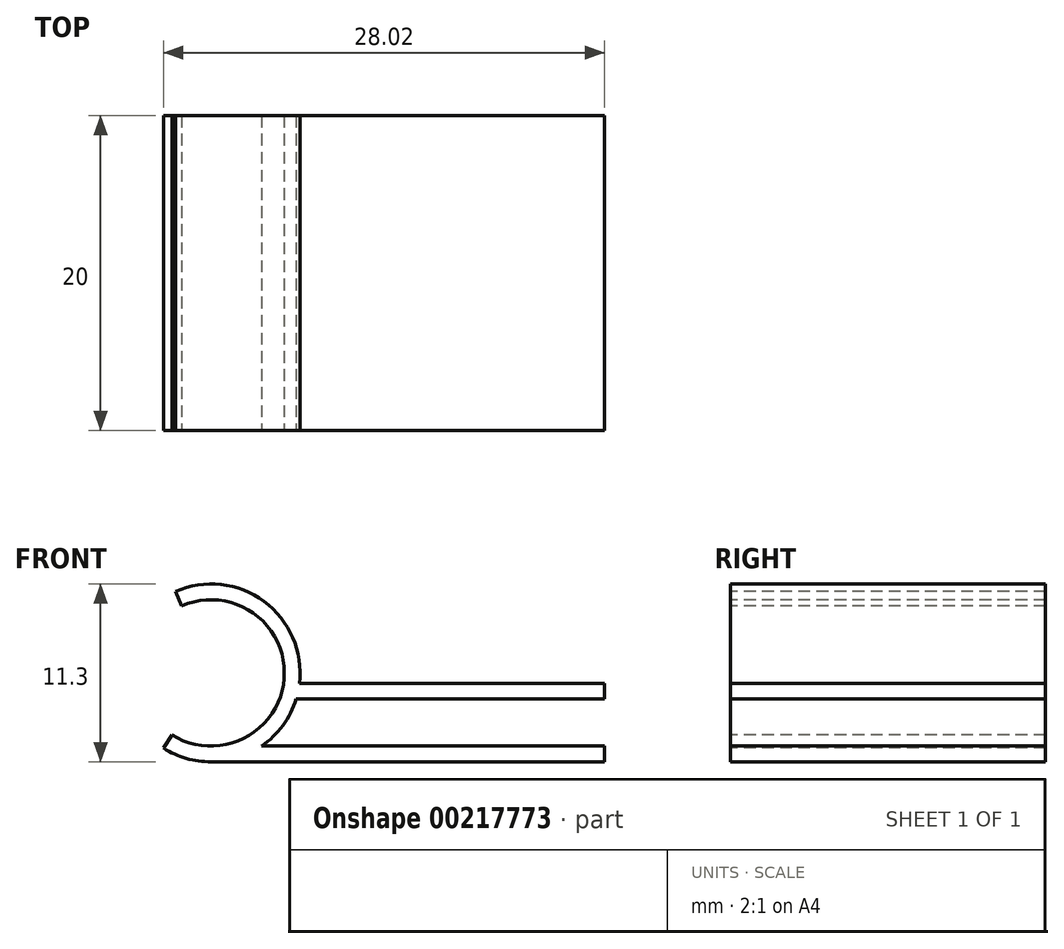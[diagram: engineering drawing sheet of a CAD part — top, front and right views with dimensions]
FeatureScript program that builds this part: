
annotation { "Feature Type Name" : "Feature", "Feature Type Description" : "" }
export const myFeature = defineFeature(function(context is Context, id is Id, definition is map)
    precondition{}
    {
        {
            var Q0;
            Q0=qCreatedBy(makeId("Front.planeOp"),FACE);
            var sketch = newSketch(context, id + "F0", { "sketchPlane" : qUnion([Q0])});
            skCircle(sketch, "E0", {"center": v(11.88, 1.65) * mm, "radius": 4.65 * mm});
            skCircle(sketch, "E1", {"center": v(11.88, 1.65) * mm, "radius": 5.65 * mm});
            skLineSegment(sketch, "E2.bottom", {"start": v(11.88, -4) * mm, "end": v(36.88, -4) * mm});
            skLineSegment(sketch, "E2.top", {"start": v(11.88, -3) * mm, "end": v(36.88, -3) * mm});
            skLineSegment(sketch, "E2.left", {"start": v(11.88, -4) * mm, "end": v(11.88, -3) * mm});
            skLineSegment(sketch, "E2.right", {"start": v(36.88, -4) * mm, "end": v(36.88, -3) * mm});
            skLineSegment(sketch, "E3.bottom", {"start": v(36.88, 0) * mm, "end": v(16.49, 0) * mm});
            skLineSegment(sketch, "E3.top", {"start": v(36.88, 1) * mm, "end": v(16.49, 1) * mm});
            skLineSegment(sketch, "E3.left", {"start": v(36.88, 0) * mm, "end": v(36.88, 1) * mm});
            skLineSegment(sketch, "E3.right", {"start": v(16.49, 0) * mm, "end": v(16.49, 1) * mm});
            skLineSegment(sketch, "E4", {"start": v(6.8, 13.29) * mm, "end": v(11.88, 1.65) * mm});
            skLineSegment(sketch, "E5", {"start": v(11.88, 1.65) * mm, "end": v(5.08, -9.07) * mm});
            skLineSegment(sketch, "E6", {"start": v(6.8, 13.29) * mm, "end": v(5.08, -9.07) * mm});
            skSolve(sketch);
        }
        {
            var Q0;
            {var subQ3=sQuery(id+"F0.wireOp",EDGE,"E4");var subQ5=sQuery(id+"F0.wireOp",EDGE,"E1");var subQ6=makeQuery(id+"F0.imprint","INTERSECT",VERTEX,{"derivedFrom":[subQ5,subQ3]});Q0=makeQuery(id+"F0.imprint","IMPRINT",FACE,{"disambiguationData":[TD([[makeQuery(id+"F0.imprint","IMPRINT",EDGE,{"disambiguationData":[TD([[subQ6,1.0]])],"derivedFrom":subQ5}),1.0]])]});}
            var Q1;
            {var subQ7=sQuery(id+"F0.wireOp",EDGE,"E3.right");Q1=makeQuery(id+"F0.imprint","IMPRINT",FACE,{"disambiguationData":[TD([[makeQuery(id+"F0.imprint","IMPRINT",EDGE,{"derivedFrom":subQ7}),1.0]])]});}
            var Q2;
            {var subQ5=sQuery(id+"F0.wireOp",EDGE,"E3.right");Q2=makeQuery(id+"F0.imprint","IMPRINT",FACE,{"disambiguationData":[TD([[makeQuery(id+"F0.imprint","IMPRINT",EDGE,{"derivedFrom":subQ5}),-1.0]])]});}
            var Q3;
            {var subQ5=sQuery(id+"F0.wireOp",EDGE,"E3.left");Q3=makeQuery(id+"F0.imprint","IMPRINT",FACE,{"disambiguationData":[TD([[makeQuery(id+"F0.imprint","IMPRINT",EDGE,{"derivedFrom":subQ5}),1.0]])]});}
            var Q4;
            {var subQ0=sQuery(id+"F0.wireOp",EDGE,"E2.bottom");Q4=makeQuery(id+"F0.imprint","IMPRINT",FACE,{"disambiguationData":[TD([[makeQuery(id+"F0.imprint","IMPRINT",EDGE,{"derivedFrom":subQ0}),1.0]])]});}
            var Q5;
            {var subQ0=sQuery(id+"F0.wireOp",EDGE,"E2.left");Q5=makeQuery(id+"F0.imprint","IMPRINT",FACE,{"disambiguationData":[TD([[makeQuery(id+"F0.imprint","IMPRINT",EDGE,{"derivedFrom":subQ0}),-1.0]])]});}
            var Q6;
            {var subQ0=sQuery(id+"F0.wireOp",EDGE,"E2.left");Q6=makeQuery(id+"F0.imprint","IMPRINT",FACE,{"disambiguationData":[TD([[makeQuery(id+"F0.imprint","IMPRINT",EDGE,{"derivedFrom":subQ0}),1.0]])]});}
            extrude(context, id + "F1", {"entities" : qUnion([Q0, Q1, Q2, Q3, Q4, Q5, Q6]), "oppositeDirection" : true, "depth" : 20 * mm});
        }
    });
